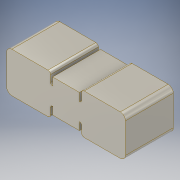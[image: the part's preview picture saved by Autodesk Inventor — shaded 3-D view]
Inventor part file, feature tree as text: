
AUTODESK INVENTOR PART (.ipt)
format: ipt  version: 2017 (Build 210142000, 142)  size: 135,680 bytes
history: native  units: in
note: dims shown in document units (in); Inventor stores cm internally (conversion verified against a paired STEP export)
features: extrude x1, sketch x1
ambient origin geometry x8: Origin, YZ Plane, XZ Plane, XY Plane, X Axis, Y Axis, Z Axis, Center Point
bodies: Solid1 (feature_tree)
feature tree (2):
  extrude  "Extrusion1"  Depth=0.85in
  sketch  "Sketch1"  dims[d1=0.39in d2=0.85in d3=0.22in d4=0.04in d5=0.32in d6=0.1in d7=0.05in d8=0.04in d9=0.926in d10=0.0in]
